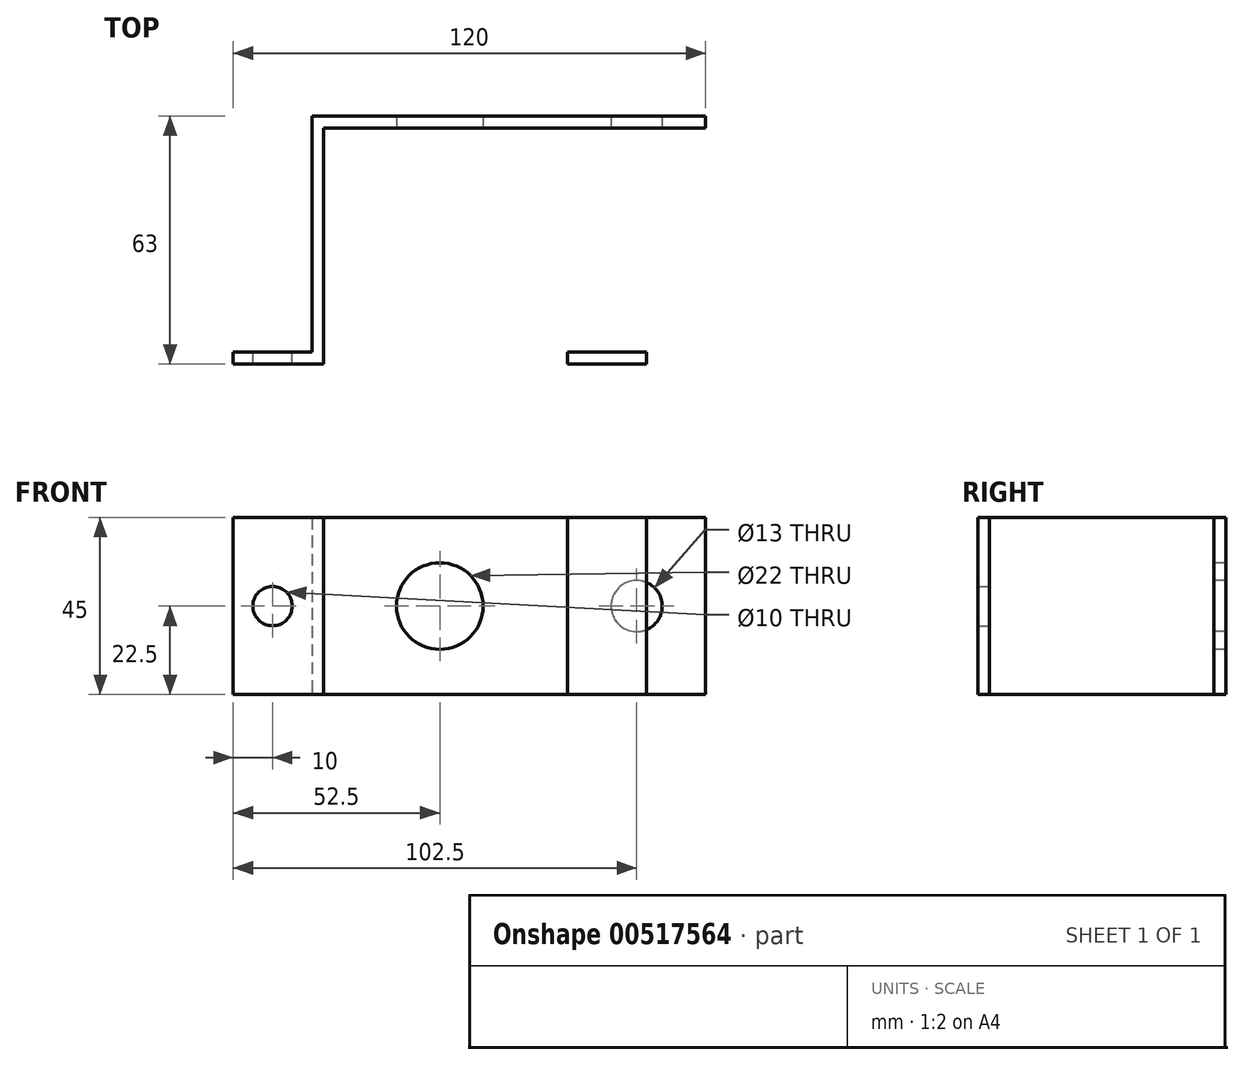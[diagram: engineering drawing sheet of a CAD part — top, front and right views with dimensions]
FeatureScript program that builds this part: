
annotation { "Feature Type Name" : "Feature", "Feature Type Description" : "" }
export const myFeature = defineFeature(function(context is Context, id is Id, definition is map)
    precondition{}
    {
        {
            var Q0;
            Q0=qCreatedBy(makeId("Top.planeOp"),FACE);
            var sketch = newSketch(context, id + "F0", { "sketchPlane" : qUnion([Q0])});
            skLineSegment(sketch, "E0", {"start": v(0, 0) * mm, "end": v(50, 0) * mm});
            skLineSegment(sketch, "E1", {"start": v(0, 0) * mm, "end": v(-50, 0) * mm});
            skLineSegment(sketch, "E2", {"start": v(-50, 0) * mm, "end": v(-50, 3) * mm});
            skLineSegment(sketch, "E3", {"start": v(-50, 3) * mm, "end": v(50, 3) * mm});
            skLineSegment(sketch, "E4", {"start": v(50, 3) * mm, "end": v(50, 0) * mm});
            skPoint(sketch, "E5", {"position": v(0, 0) * mm});
            skLineSegment(sketch, "E6", {"start": v(0, 0) * mm, "end": v(15, 0) * mm});
            skLineSegment(sketch, "E7", {"start": v(15, 0) * mm, "end": v(15, -60) * mm});
            skLineSegment(sketch, "E8", {"start": v(15, -60) * mm, "end": v(12, -60) * mm});
            skLineSegment(sketch, "E9", {"start": v(12, -60) * mm, "end": v(12, 0) * mm});
            skLineSegment(sketch, "E10", {"start": v(-50, 0) * mm, "end": v(-50, -60) * mm});
            skLineSegment(sketch, "E11", {"start": v(-50, -60) * mm, "end": v(-47, -60) * mm});
            skLineSegment(sketch, "E12", {"start": v(-47, -60) * mm, "end": v(-47, 0) * mm});
            skLineSegment(sketch, "E13", {"start": v(-47, 0) * mm, "end": v(12, 0) * mm});
            skPoint(sketch, "E14", {"position": v(-17.5, 0) * mm});
            skLineSegment(sketch, "E15", {"start": v(15, 0) * mm, "end": v(50, 0) * mm});
            skPoint(sketch, "E16", {"position": v(32.5, 0) * mm});
            skLineSegment(sketch, "E17", {"start": v(15, -60) * mm, "end": v(35, -60) * mm});
            skLineSegment(sketch, "E18", {"start": v(35, -60) * mm, "end": v(35, -57) * mm});
            skLineSegment(sketch, "E19", {"start": v(35, -57) * mm, "end": v(15, -57) * mm});
            skLineSegment(sketch, "E20", {"start": v(-50, -60) * mm, "end": v(-70, -60) * mm});
            skLineSegment(sketch, "E21", {"start": v(-70, -60) * mm, "end": v(-70, -57) * mm});
            skLineSegment(sketch, "E22", {"start": v(-70, -57) * mm, "end": v(-50, -57) * mm});
            skSolve(sketch);
        }
        {
            var Q0;
            Q0=qCreatedBy(makeId("Front.planeOp"),FACE);
            var sketch = newSketch(context, id + "F1", { "sketchPlane" : qUnion([Q0])});
            skPoint(sketch, "E23", {"position": v(-50, 0) * mm});
            skPoint(sketch, "E24", {"position": v(15, 0) * mm});
            skPoint(sketch, "E25", {"position": v(12, 0) * mm});
            skPoint(sketch, "E26", {"position": v(-17.5, 0) * mm});
            skPoint(sketch, "E27", {"position": v(32.5, 0) * mm});
            skSolve(sketch);
        }
        {
            var Q0;
            {var subQ1=sQuery(id+"F0.wireOp",EDGE,"E1");Q0=makeQuery(id+"F0.imprint","IMPRINT",FACE,{"disambiguationData":[TD([[makeQuery(id+"F0.imprint","IMPRINT",EDGE,{"derivedFrom":subQ1}),-1.0]])]});}
            var Q1;
            {var subQ3=sQuery(id+"F0.wireOp",EDGE,"E6");Q1=makeQuery(id+"F0.imprint","IMPRINT",FACE,{"disambiguationData":[TD([[makeQuery(id+"F0.imprint","IMPRINT",EDGE,{"derivedFrom":subQ3}),-1.0]])]});}
            var Q2;
            {var subQ1=sQuery(id+"F0.wireOp",EDGE,"E1");Q2=makeQuery(id+"F0.imprint","IMPRINT",FACE,{"disambiguationData":[TD([[makeQuery(id+"F0.imprint","IMPRINT",EDGE,{"derivedFrom":subQ1}),1.0]])]});}
            var Q3;
            {var subQ0=sQuery(id+"F0.wireOp",EDGE,"E20");Q3=makeQuery(id+"F0.imprint","IMPRINT",FACE,{"disambiguationData":[TD([[makeQuery(id+"F0.imprint","IMPRINT",EDGE,{"derivedFrom":subQ0}),-1.0]])]});}
            var Q4;
            {var subQ0=sQuery(id+"F0.wireOp",EDGE,"E17");Q4=makeQuery(id+"F0.imprint","IMPRINT",FACE,{"disambiguationData":[TD([[makeQuery(id+"F0.imprint","IMPRINT",EDGE,{"derivedFrom":subQ0}),1.0]])]});}
            extrude(context, id + "F2", {"entities" : qUnion([Q0, Q1, Q2, Q3, Q4]), "endBound" : BoundingType.SYMMETRIC, "depth" : 45 * mm, "offsetDistance" : 25 * mm});
        }
        {
            var Q0;
            Q0=sQuery(id+"F1.wireOp",VERTEX,"AHlc7qOz-VzAY-R7JC-ZmUR-b7LxQJLUYPv3.center");
            var Q1;
            Q1=sQuery(id+"F1.wireOp",VERTEX,"4537cdb1-fe09-4adb-9d55-388c6a81b586");
            var Q2;
            Q2=sQuery(id+"F1.wireOp",VERTEX,"E27");
            var Q3;
            Q3=makeQuery(id+"F2.opExtrude","SWEPT_BODY",BODY,{"disambiguationData":[OSD([sQuery(id+"F0.wireOp",EDGE,"E2"),sQuery(id+"F0.wireOp",EDGE,"E3"),sQuery(id+"F0.wireOp",EDGE,"E4"),sQuery(id+"F0.wireOp",EDGE,"E7"),sQuery(id+"F0.wireOp",EDGE,"E8"),sQuery(id+"F0.wireOp",EDGE,"E9"),sQuery(id+"F0.wireOp",EDGE,"E10"),sQuery(id+"F0.wireOp",EDGE,"E11"),sQuery(id+"F0.wireOp",EDGE,"E12"),sQuery(id+"F0.wireOp",EDGE,"E13"),sQuery(id+"F0.wireOp",EDGE,"E15"),sQuery(id+"F0.wireOp",EDGE,"E17"),sQuery(id+"F0.wireOp",EDGE,"E18"),sQuery(id+"F0.wireOp",EDGE,"E19"),sQuery(id+"F0.wireOp",EDGE,"E20"),sQuery(id+"F0.wireOp",EDGE,"E21"),sQuery(id+"F0.wireOp",EDGE,"E22")])]});
            hole(context, id + "F3", {"style" : HoleStyle.SIMPLE, "endStyle" : HoleEndStyle.BLIND, "holeDiameter" : 13 * mm, "holeDepth" : 10 * mm, "isTappedThrough" : true, "tappedDepth" : 12 * mm, "tapClearance" : 3, "locations" : qUnion([Q0, Q1, Q2]), "scope" : qUnion([Q3])});
        }
        {
            var Q0;
            Q0=sQuery(id+"F1.wireOp",VERTEX,"KyEE0Y6f-hmQ8-Et8X-ylQV-ebCA5YQ7oy5M.center");
            var Q1;
            Q1=sQuery(id+"F1.wireOp",VERTEX,"fe93fc6c-313b-4e99-9fe0-ca83af8035da");
            var Q2;
            Q2=sQuery(id+"F1.wireOp",VERTEX,"E26");
            var Q3;
            Q3=makeQuery(id+"F2.opExtrude","SWEPT_BODY",BODY,{"disambiguationData":[OSD([sQuery(id+"F0.wireOp",EDGE,"E2"),sQuery(id+"F0.wireOp",EDGE,"E3"),sQuery(id+"F0.wireOp",EDGE,"E4"),sQuery(id+"F0.wireOp",EDGE,"E7"),sQuery(id+"F0.wireOp",EDGE,"E8"),sQuery(id+"F0.wireOp",EDGE,"E9"),sQuery(id+"F0.wireOp",EDGE,"E10"),sQuery(id+"F0.wireOp",EDGE,"E11"),sQuery(id+"F0.wireOp",EDGE,"E12"),sQuery(id+"F0.wireOp",EDGE,"E13"),sQuery(id+"F0.wireOp",EDGE,"E15"),sQuery(id+"F0.wireOp",EDGE,"E17"),sQuery(id+"F0.wireOp",EDGE,"E18"),sQuery(id+"F0.wireOp",EDGE,"E19"),sQuery(id+"F0.wireOp",EDGE,"E20"),sQuery(id+"F0.wireOp",EDGE,"E21"),sQuery(id+"F0.wireOp",EDGE,"E22")])]});
            hole(context, id + "F4", {"style" : HoleStyle.SIMPLE, "endStyle" : HoleEndStyle.BLIND, "holeDiameter" : 22 * mm, "holeDepth" : 10 * mm, "isTappedThrough" : true, "tappedDepth" : 12 * mm, "tapClearance" : 3, "locations" : qUnion([Q0, Q1, Q2]), "scope" : qUnion([Q3])});
        }
        {
            var Q0;
            Q0=makeQuery(id+"F2.opExtrude","SWEPT_FACE",FACE,{"disambiguationData":[OSD([sQuery(id+"F0.wireOp",EDGE,"E22")])]});
            var sketch = newSketch(context, id + "F5", { "sketchPlane" : qUnion([Q0])});
            skPoint(sketch, "E28", {"position": v(60, 0) * mm});
            skPoint(sketch, "E28.positionSnap0", {"position": v(60, -22.5) * mm});
            skSolve(sketch);
        }
        {
            var Q0;
            Q0=makeQuery(id+"F2.opExtrude","SWEPT_FACE",FACE,{"disambiguationData":[OSD([sQuery(id+"F0.wireOp",EDGE,"E19")])]});
            var sketch = newSketch(context, id + "F6", { "sketchPlane" : qUnion([Q0])});
            skPoint(sketch, "E29", {"position": v(-25, 0) * mm});
            skPoint(sketch, "E29.positionSnap0", {"position": v(-25, -22.5) * mm});
            skSolve(sketch);
        }
        {
            var Q0;
            Q0=sQuery(id+"FCtxovEqMnNV0x4_1.wireOp",VERTEX,"71bf34a9-dc11-4b16-81df-6541852ce4bb");
            var Q1;
            Q1=sQuery(id+"FQgqvmxPmDdWZKs_1.wireOp",VERTEX,"8a05ef2e-bedd-437f-a8d4-7204653be142");
            var Q2;
            Q2=sQuery(id+"F6.wireOp",VERTEX,"E29");
            var Q3;
            Q3=sQuery(id+"F5.wireOp",VERTEX,"E28");
            var Q4;
            Q4=makeQuery(id+"F2.opExtrude","SWEPT_BODY",BODY,{"disambiguationData":[OSD([sQuery(id+"F0.wireOp",EDGE,"E2"),sQuery(id+"F0.wireOp",EDGE,"E3"),sQuery(id+"F0.wireOp",EDGE,"E4"),sQuery(id+"F0.wireOp",EDGE,"E7"),sQuery(id+"F0.wireOp",EDGE,"E8"),sQuery(id+"F0.wireOp",EDGE,"E9"),sQuery(id+"F0.wireOp",EDGE,"E10"),sQuery(id+"F0.wireOp",EDGE,"E11"),sQuery(id+"F0.wireOp",EDGE,"E12"),sQuery(id+"F0.wireOp",EDGE,"E13"),sQuery(id+"F0.wireOp",EDGE,"E15"),sQuery(id+"F0.wireOp",EDGE,"E17"),sQuery(id+"F0.wireOp",EDGE,"E18"),sQuery(id+"F0.wireOp",EDGE,"E19"),sQuery(id+"F0.wireOp",EDGE,"E20"),sQuery(id+"F0.wireOp",EDGE,"E21"),sQuery(id+"F0.wireOp",EDGE,"E22")])]});
            hole(context, id + "F7", {"style" : HoleStyle.SIMPLE, "endStyle" : HoleEndStyle.BLIND, "holeDiameter" : 10 * mm, "holeDepth" : 10 * mm, "isTappedThrough" : true, "tappedDepth" : 12 * mm, "tapClearance" : 3, "locations" : qUnion([Q0, Q1, Q2, Q3]), "scope" : qUnion([Q4])});
        }
    });
